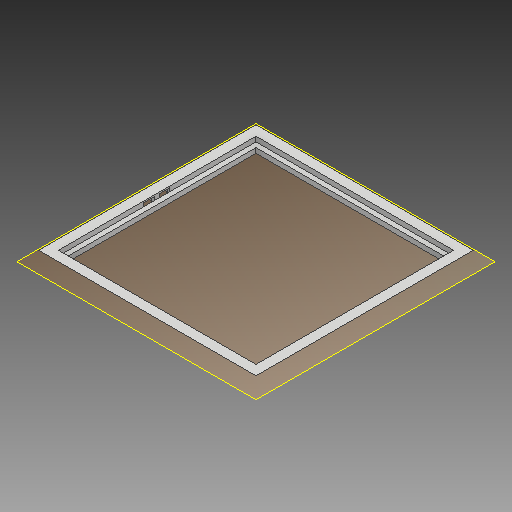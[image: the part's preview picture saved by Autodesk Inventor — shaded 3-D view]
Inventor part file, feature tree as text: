
AUTODESK INVENTOR PART (.ipt)
format: ipt  version: 2018.2 (Build 222227000, 227)  size: 143,360 bytes
history: native  units: mm
features: reference x13, other x7, extrude x3, sketch x3, chamfer x1, plane x1
ambient origin geometry x8: Origin, YZ Plane, XZ Plane, XY Plane, X Axis, Y Axis, Z Axis, Center Point
bodies: Volumenkörper1 (feature_tree)
feature tree (28):
  extrude  "Extrusion1"  Depth=20.0mm TaperAngle=45.0deg
  chamfer  "Fase1"  Distance=17.0mm
  plane  "Arbeitsebene1"
  extrude  "Extrusion2"  Depth=10.0mm
  extrude  "Extrusion3"  Depth=10.0mm
  sketch  "Skizze1"  dims[d0=20.0mm d1=0.0mm d2=20.0mm d3=2.0mm d4=45.0deg]
  reference  "Referenz1"
  reference  "Referenz2"
  reference  "Referenz3"
  reference  "Referenz4"
  reference  "Referenz5"
  sketch  "Skizze3"  dims[d5=-20.0mm d6=17.0mm d7=0.0mm]
  reference  "Referenz12"
  reference  "Referenz13"
  reference  "Referenz14"
  reference  "Referenz15"
  reference  "Referenz16"
  reference  "Referenz17"
  reference  "Referenz18"
  reference  "Referenz19"
  sketch  "Skizze5"  dims[d8=10.0mm d9=10.0mm d10=10.0mm d11=10.0mm d12=10.0mm d13=0.0mm]
  parser-record x1  (decoder bookkeeping rows leaked as tree rows — omitted from the tree; the rows remain in map.json)
  other  "SmartCube_Quadratisch.iam"
  other  "Wand2_MIR:1"
  other  "Wand1:1"
  other  "Wand1_MIR:1"
  other  "Wand2:1"
  other  "PV_Modul:1"
note: 1 file-system path scrubbed to <path> (originals preserved in map.json)
